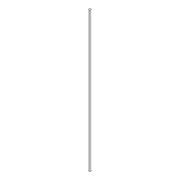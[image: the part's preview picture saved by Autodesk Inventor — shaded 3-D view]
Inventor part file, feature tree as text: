
AUTODESK INVENTOR PART (.ipt)
format: ipt  version: 2020 (Build 240168000, 168)  size: 69,632 bytes
history: native  units: mm
features: other x1, extrude x1, sketch x1
ambient origin geometry x8: Origin, YZ Plane, XZ Plane, XY Plane, X Axis, Y Axis, Z Axis, Center Point
bodies: Body1 (feature_tree)
feature tree (3):
  other  "Sólido1"
  extrude  "Extrusão1"  Depth=130.0mm TaperAngle=0.0deg
  sketch  "Esboço1"  dims[d0=2.0mm d1=130.0mm d2=0.0mm]
